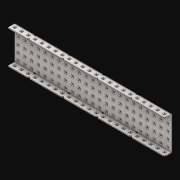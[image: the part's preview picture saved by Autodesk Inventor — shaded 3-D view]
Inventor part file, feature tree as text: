
AUTODESK INVENTOR PART (.ipt)
format: ipt  version: 2021 (Build 250183000, 183)  size: 3,513,856 bytes
history: native  units: in
note: dims shown in document units (in); Inventor stores cm internally (conversion verified against a paired STEP export)
features: extrude x162, other x161, sketch x4, thicken_offset x3, pattern_linear x3, imported_body x1
ambient origin geometry x8: Origin, YZ Plane, XZ Plane, XY Plane, X Axis, Y Axis, Z Axis, Center Point
bodies: Solid1 (feature_tree)
feature tree (334):
  thicken_offset  "Thicken1"
  thicken_offset  "Thicken2"
  thicken_offset  "Thicken3"
  pattern_linear  "Rectangular Pattern1"  Spacing1=0.001in  [1 undecoded]
  pattern_linear  "Rectangular Pattern2"  Spacing1=0.001in  [1 undecoded]
  pattern_linear  "Rectangular Pattern3"  Spacing1=0.182in  [1 undecoded]
  extrude  "Extrusion1"  Depth=0.063in TaperAngle=0.0deg
  sketch  "Sketch1"  dims[d0=0.001in]
  other  "Srf1"
  sketch  "Sketch2"  dims[d1=0.001in]
  other  "Srf2"
  sketch  "Sketch3"  dims[d2=0.001in]
  other  "Srf3"
  other  "Srf4"
  other  "Srf5"
  other  "Srf6"
  other  "Srf7"
  other  "Srf8"
  other  "Srf9"
  other  "Srf10"
  other  "Srf11"
  other  "Srf12"
  other  "Srf13"
  other  "Srf14"
  other  "Srf15"
  other  "Srf16"
  other  "Srf17"
  other  "Srf18"
  other  "Srf19"
  other  "Srf20"
  other  "Srf21"
  other  "Srf22"
  other  "Srf23"
  other  "Srf24"
  other  "Srf25"
  other  "Srf38"
  other  "Srf39"
  other  "Srf40"
  other  "Srf41"
  other  "Srf42"
  other  "Srf43"
  other  "Srf44"
  other  "Srf45"
  other  "Srf46"
  other  "Srf47"
  other  "Srf48"
  other  "Srf49"
  other  "Srf50"
  other  "Srf51"
  other  "Srf52"
  other  "Srf53"
  other  "Srf54"
  other  "Srf55"
  other  "Srf56"
  other  "Srf57"
  other  "Srf58"
  other  "Srf59"
  other  "Srf72"
  other  "Srf73"
  other  "Srf74"
  other  "Srf75"
  other  "Srf76"
  other  "Srf77"
  other  "Srf78"
  other  "Srf79"
  other  "Srf80"
  other  "Srf81"
  other  "Srf82"
  other  "Srf83"
  other  "Srf84"
  other  "Srf85"
  other  "Srf86"
  other  "Srf87"
  other  "Srf88"
  other  "Srf89"
  other  "Srf90"
  other  "Srf91"
  other  "Srf92"
  other  "Srf93"
  other  "Srf106"
  other  "Srf107"
  other  "Srf108"
  other  "Srf109"
  other  "Srf110"
  other  "Srf111"
  other  "Srf112"
  other  "Srf113"
  other  "Srf114"
  other  "Srf115"
  other  "Srf116"
  other  "Srf117"
  other  "Srf118"
  other  "Srf119"
  other  "Srf120"
  other  "Srf121"
  other  "Srf122"
  other  "Srf123"
  other  "Srf124"
  other  "Srf125"
  other  "Srf126"
  other  "Srf127"
  other  "Srf128"
  other  "Srf141"
  other  "Srf142"
  other  "Srf143"
  other  "Srf144"
  other  "Srf145"
  other  "Srf146"
  other  "Srf147"
  other  "Srf148"
  other  "Srf149"
  other  "Srf150"
  other  "Srf151"
  other  "Srf152"
  other  "Srf153"
  other  "Srf154"
  other  "Srf155"
  other  "Srf156"
  other  "Srf157"
  other  "Srf158"
  other  "Srf159"
  other  "Srf160"
  other  "Srf161"
  other  "Srf162"
  other  "Srf163"
  other  "Srf176"
  other  "Srf177"
  other  "Srf178"
  other  "Srf179"
  other  "Srf180"
  other  "Srf181"
  other  "Srf182"
  other  "Srf183"
  other  "Srf184"
  other  "Srf185"
  other  "Srf186"
  other  "Srf187"
  other  "Srf188"
  other  "Srf189"
  other  "Srf190"
  other  "Srf191"
  other  "Srf192"
  other  "Srf193"
  other  "Srf194"
  other  "Srf195"
  other  "Srf196"
  other  "Srf197"
  other  "Srf198"
  other  "Srf211"
  other  "Srf212"
  other  "Srf213"
  other  "Srf214"
  other  "Srf215"
  other  "Srf216"
  other  "Srf217"
  other  "Srf218"
  other  "Srf219"
  other  "Srf220"
  other  "Srf221"
  other  "Srf222"
  other  "Srf223"
  other  "Srf224"
  other  "Srf225"
  other  "Srf226"
  other  "Srf227"
  other  "Srf228"
  other  "Srf229"
  other  "Srf230"
  other  "Srf231"
  other  "Srf232"
  other  "Srf233"
  sketch  "Sketch4"  dims[d3=0.001in d4=0.001in d5=0.001in d6=0.182in d7=0.063in d8=0.0in d9=0.182in d10=0.063in d11=0.0in d12=0.182in d13=0.063in d14=0.0in d17=0.5in d18=9.0551in d20=0.5in d21=9.0551in d23=0.5in d24=1.9685in d26=0.5in d27=6.0in d28=0.0in]
  imported_body  "Imported1"
  extrude  "ExtrusionSrf1"  Depth=6.0in
  extrude  "ExtrusionSrf2"  Depth=0.063in TaperAngle=0.0deg
  extrude  "ExtrusionSrf3"  Depth=6.0in
  extrude  "ExtrusionSrf4"  Depth=0.063in TaperAngle=0.0deg
  extrude  "ExtrusionSrf5"  Depth=0.5in
  extrude  "ExtrusionSrf6"  Depth=6.0in
  extrude  "ExtrusionSrf7"  Depth=0.5in
  extrude  "ExtrusionSrf8"  Depth=6.0in
  extrude  "ExtrusionSrf9"  Depth=0.5in
  extrude  "ExtrusionSrf10"  Depth=0.5in
  extrude  "ExtrusionSrf11"  Depth=6.0in
  extrude  "ExtrusionSrf12"  TaperAngle=0.0deg  [1 undecoded]
  extrude  "ExtrusionSrf13"  [1 undecoded]
  extrude  "ExtrusionSrf14"  [1 undecoded]
  extrude  "ExtrusionSrf15"  [1 undecoded]
  extrude  "ExtrusionSrf16"  [1 undecoded]
  extrude  "ExtrusionSrf17"  [1 undecoded]
  extrude  "ExtrusionSrf18"  [1 undecoded]
  extrude  "ExtrusionSrf19"  [1 undecoded]
  extrude  "ExtrusionSrf20"  [1 undecoded]
  extrude  "ExtrusionSrf21"  [1 undecoded]
  extrude  "ExtrusionSrf22"  [1 undecoded]
  extrude  "ExtrusionSrf23"  [1 undecoded]
  extrude  "ExtrusionSrf24"  [1 undecoded]
  extrude  "ExtrusionSrf25"  [1 undecoded]
  extrude  "ExtrusionSrf38"  [1 undecoded]
  extrude  "ExtrusionSrf39"  [1 undecoded]
  extrude  "ExtrusionSrf40"  [1 undecoded]
  extrude  "ExtrusionSrf41"  [1 undecoded]
  extrude  "ExtrusionSrf42"  [1 undecoded]
  extrude  "ExtrusionSrf43"  [1 undecoded]
  extrude  "ExtrusionSrf44"  [1 undecoded]
  extrude  "ExtrusionSrf45"  [1 undecoded]
  extrude  "ExtrusionSrf46"  [1 undecoded]
  extrude  "ExtrusionSrf47"  [1 undecoded]
  extrude  "ExtrusionSrf48"  [1 undecoded]
  extrude  "ExtrusionSrf49"  [1 undecoded]
  extrude  "ExtrusionSrf50"  [1 undecoded]
  extrude  "ExtrusionSrf51"  [1 undecoded]
  extrude  "ExtrusionSrf52"  [1 undecoded]
  extrude  "ExtrusionSrf53"  [1 undecoded]
  extrude  "ExtrusionSrf54"  [1 undecoded]
  extrude  "ExtrusionSrf55"  [1 undecoded]
  extrude  "ExtrusionSrf56"  [1 undecoded]
  extrude  "ExtrusionSrf57"  [1 undecoded]
  extrude  "ExtrusionSrf58"  [1 undecoded]
  extrude  "ExtrusionSrf59"  [1 undecoded]
  extrude  "ExtrusionSrf72"  [1 undecoded]
  extrude  "ExtrusionSrf73"  [1 undecoded]
  extrude  "ExtrusionSrf74"  [1 undecoded]
  extrude  "ExtrusionSrf75"  [1 undecoded]
  extrude  "ExtrusionSrf76"  [1 undecoded]
  extrude  "ExtrusionSrf77"  [1 undecoded]
  extrude  "ExtrusionSrf78"  [1 undecoded]
  extrude  "ExtrusionSrf79"  [1 undecoded]
  extrude  "ExtrusionSrf80"  [1 undecoded]
  extrude  "ExtrusionSrf81"  [1 undecoded]
  extrude  "ExtrusionSrf82"  [1 undecoded]
  extrude  "ExtrusionSrf83"  [1 undecoded]
  extrude  "ExtrusionSrf84"  [1 undecoded]
  extrude  "ExtrusionSrf85"  [1 undecoded]
  extrude  "ExtrusionSrf86"  [1 undecoded]
  extrude  "ExtrusionSrf87"  [1 undecoded]
  extrude  "ExtrusionSrf88"  [1 undecoded]
  extrude  "ExtrusionSrf89"  [1 undecoded]
  extrude  "ExtrusionSrf90"  [1 undecoded]
  extrude  "ExtrusionSrf91"  [1 undecoded]
  extrude  "ExtrusionSrf92"  [1 undecoded]
  extrude  "ExtrusionSrf93"  [1 undecoded]
  extrude  "ExtrusionSrf106"  [1 undecoded]
  extrude  "ExtrusionSrf107"  [1 undecoded]
  extrude  "ExtrusionSrf108"  [1 undecoded]
  extrude  "ExtrusionSrf109"  [1 undecoded]
  extrude  "ExtrusionSrf110"  [1 undecoded]
  extrude  "ExtrusionSrf111"  [1 undecoded]
  extrude  "ExtrusionSrf112"  [1 undecoded]
  extrude  "ExtrusionSrf113"  [1 undecoded]
  extrude  "ExtrusionSrf114"  [1 undecoded]
  extrude  "ExtrusionSrf115"  [1 undecoded]
  extrude  "ExtrusionSrf116"  [1 undecoded]
  extrude  "ExtrusionSrf117"  [1 undecoded]
  extrude  "ExtrusionSrf118"  [1 undecoded]
  extrude  "ExtrusionSrf119"  [1 undecoded]
  extrude  "ExtrusionSrf120"  [1 undecoded]
  extrude  "ExtrusionSrf121"  [1 undecoded]
  extrude  "ExtrusionSrf122"  [1 undecoded]
  extrude  "ExtrusionSrf123"  [1 undecoded]
  extrude  "ExtrusionSrf124"  [1 undecoded]
  extrude  "ExtrusionSrf125"  [1 undecoded]
  extrude  "ExtrusionSrf126"  [1 undecoded]
  extrude  "ExtrusionSrf127"  [1 undecoded]
  extrude  "ExtrusionSrf128"  [1 undecoded]
  extrude  "ExtrusionSrf141"  [1 undecoded]
  extrude  "ExtrusionSrf142"  [1 undecoded]
  extrude  "ExtrusionSrf143"  [1 undecoded]
  extrude  "ExtrusionSrf144"  [1 undecoded]
  extrude  "ExtrusionSrf145"  [1 undecoded]
  extrude  "ExtrusionSrf146"  [1 undecoded]
  extrude  "ExtrusionSrf147"  [1 undecoded]
  extrude  "ExtrusionSrf148"  [1 undecoded]
  extrude  "ExtrusionSrf149"  [1 undecoded]
  extrude  "ExtrusionSrf150"  [1 undecoded]
  extrude  "ExtrusionSrf151"  [1 undecoded]
  extrude  "ExtrusionSrf152"  [1 undecoded]
  extrude  "ExtrusionSrf153"  [1 undecoded]
  extrude  "ExtrusionSrf154"  [1 undecoded]
  extrude  "ExtrusionSrf155"  [1 undecoded]
  extrude  "ExtrusionSrf156"  [1 undecoded]
  extrude  "ExtrusionSrf157"  [1 undecoded]
  extrude  "ExtrusionSrf158"  [1 undecoded]
  extrude  "ExtrusionSrf159"  [1 undecoded]
  extrude  "ExtrusionSrf160"  [1 undecoded]
  extrude  "ExtrusionSrf161"  [1 undecoded]
  extrude  "ExtrusionSrf162"  [1 undecoded]
  extrude  "ExtrusionSrf163"  [1 undecoded]
  extrude  "ExtrusionSrf176"  [1 undecoded]
  extrude  "ExtrusionSrf177"  [1 undecoded]
  extrude  "ExtrusionSrf178"  [1 undecoded]
  extrude  "ExtrusionSrf179"  [1 undecoded]
  extrude  "ExtrusionSrf180"  [1 undecoded]
  extrude  "ExtrusionSrf181"  [1 undecoded]
  extrude  "ExtrusionSrf182"  [1 undecoded]
  extrude  "ExtrusionSrf183"  [1 undecoded]
  extrude  "ExtrusionSrf184"  [1 undecoded]
  extrude  "ExtrusionSrf185"  [1 undecoded]
  extrude  "ExtrusionSrf186"  [1 undecoded]
  extrude  "ExtrusionSrf187"  [1 undecoded]
  extrude  "ExtrusionSrf188"  [1 undecoded]
  extrude  "ExtrusionSrf189"  [1 undecoded]
  extrude  "ExtrusionSrf190"  [1 undecoded]
  extrude  "ExtrusionSrf191"  [1 undecoded]
  extrude  "ExtrusionSrf192"  [1 undecoded]
  extrude  "ExtrusionSrf193"  [1 undecoded]
  extrude  "ExtrusionSrf194"  [1 undecoded]
  extrude  "ExtrusionSrf195"  [1 undecoded]
  extrude  "ExtrusionSrf196"  [1 undecoded]
  extrude  "ExtrusionSrf197"  [1 undecoded]
  extrude  "ExtrusionSrf198"  [1 undecoded]
  extrude  "ExtrusionSrf211"  [1 undecoded]
  extrude  "ExtrusionSrf212"  [1 undecoded]
  extrude  "ExtrusionSrf213"  [1 undecoded]
  extrude  "ExtrusionSrf214"  [1 undecoded]
  extrude  "ExtrusionSrf215"  [1 undecoded]
  extrude  "ExtrusionSrf216"  [1 undecoded]
  extrude  "ExtrusionSrf217"  [1 undecoded]
  extrude  "ExtrusionSrf218"  [1 undecoded]
  extrude  "ExtrusionSrf219"  [1 undecoded]
  extrude  "ExtrusionSrf220"  [1 undecoded]
  extrude  "ExtrusionSrf221"  [1 undecoded]
  extrude  "ExtrusionSrf222"  [1 undecoded]
  extrude  "ExtrusionSrf223"  [1 undecoded]
  extrude  "ExtrusionSrf224"  [1 undecoded]
  extrude  "ExtrusionSrf225"  [1 undecoded]
  extrude  "ExtrusionSrf226"  [1 undecoded]
  extrude  "ExtrusionSrf227"  [1 undecoded]
  extrude  "ExtrusionSrf228"  [1 undecoded]
  extrude  "ExtrusionSrf229"  [1 undecoded]
  extrude  "ExtrusionSrf230"  [1 undecoded]
  extrude  "ExtrusionSrf231"  [1 undecoded]
  extrude  "ExtrusionSrf232"  [1 undecoded]
  extrude  "ExtrusionSrf233"  [1 undecoded]
note: 153 required parameter values undecoded (feature->parameter linkage not recoverable at this tier; creation-order binding heuristic only, values carry confidence <= 0.55)
